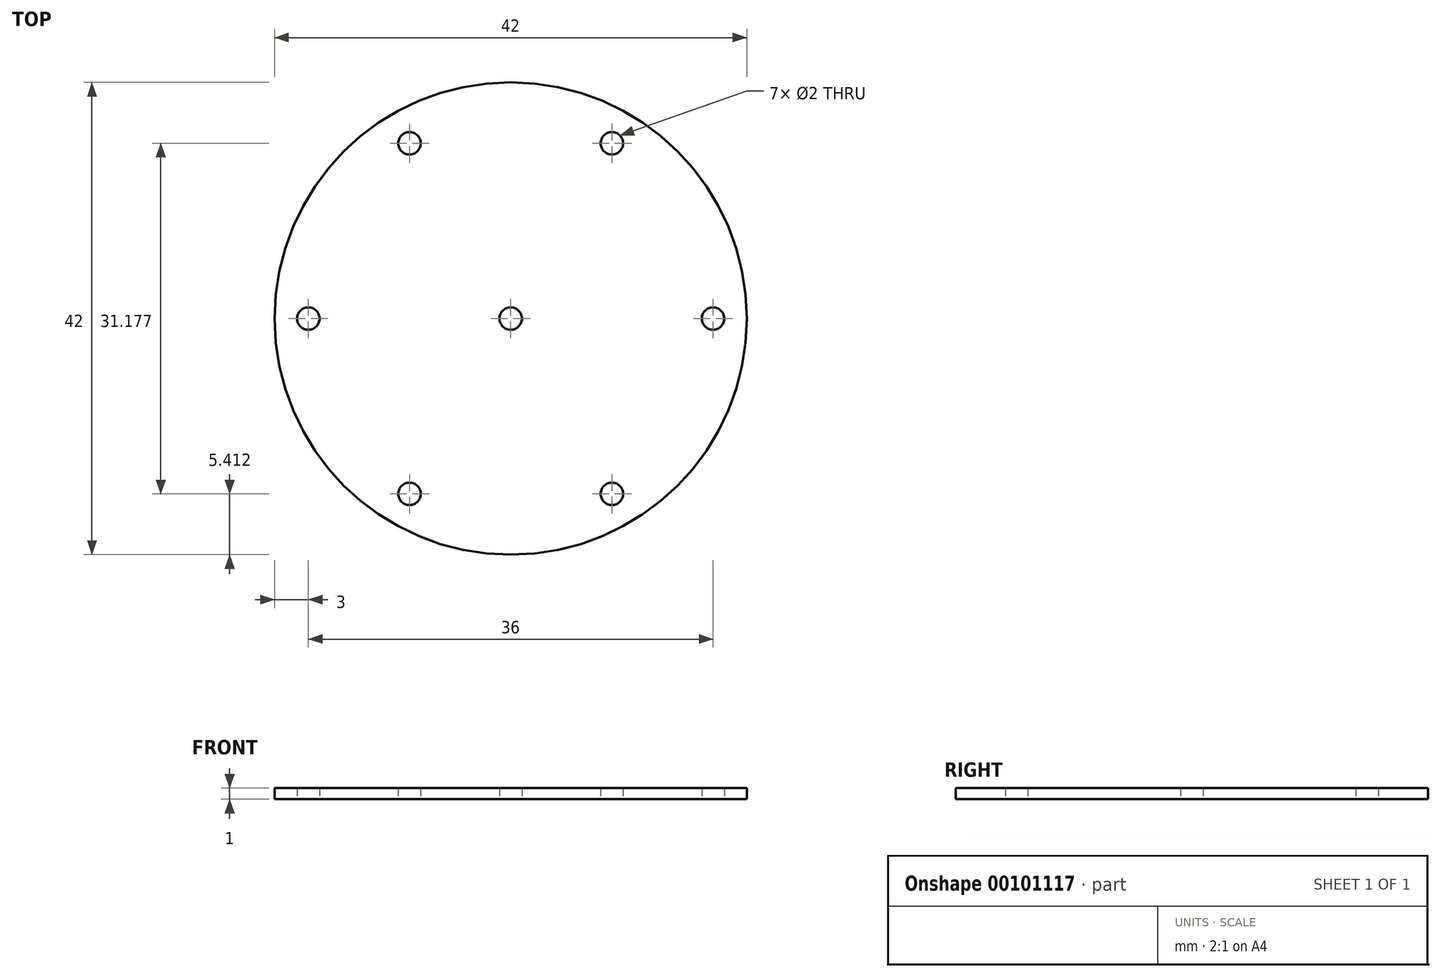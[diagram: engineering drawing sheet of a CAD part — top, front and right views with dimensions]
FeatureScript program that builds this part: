
annotation { "Feature Type Name" : "Feature", "Feature Type Description" : "" }
export const myFeature = defineFeature(function(context is Context, id is Id, definition is map)
    precondition{}
    {
        {
            var Q0;
            Q0=qCreatedBy(makeId("Top.planeOp"),FACE);
            var sketch = newSketch(context, id + "F0", { "sketchPlane" : qUnion([Q0])});
            skCircle(sketch, "E0", {"center": v(0, 0) * mm, "radius": 21 * mm});
            skPoint(sketch, "E1", {"position": v(-18, 0) * mm});
            skPoint(sketch, "E2.1.0", {"position": v(-9, -15.59) * mm});
            skPoint(sketch, "E2.2.0", {"position": v(9, -15.59) * mm});
            skPoint(sketch, "E2.3.0", {"position": v(18, 0) * mm});
            skPoint(sketch, "E2.4.0", {"position": v(9, 15.59) * mm});
            skPoint(sketch, "E2.5.0", {"position": v(-9, 15.59) * mm});
            skSolve(sketch);
        }
        {
            var Q0;
            Q0=makeQuery(id+"F0.imprint","IMPRINT",FACE,{"disambiguationData":[TD([[makeQuery(id+"F0.imprint","IMPRINT",EDGE,{"derivedFrom":sQuery(id+"F0.wireOp",EDGE,"E0")}),1.0]])]});
            var Q1;
            {var subQ0=sQuery(id+"F0.wireOp",EDGE,"3bcc4da2-44fa-43c9-b4fa-2db78715bdb7");Q1=makeQuery(id+"F0.imprint","IMPRINT",FACE,{"disambiguationData":[TD([[makeQuery(id+"F0.imprint","IMPRINT",EDGE,{"derivedFrom":subQ0}),1.0]])]});}
            var Q2;
            {var subQ0=sQuery(id+"F0.wireOp",EDGE,"ddd3eef2-9e28-40f6-aaa8-a0d2f989048d");Q2=makeQuery(id+"F0.imprint","IMPRINT",FACE,{"disambiguationData":[TD([[makeQuery(id+"F0.imprint","IMPRINT",EDGE,{"derivedFrom":subQ0}),-1.0]])]});}
            var Q3;
            Q3=makeQuery(id+"F0.imprint","IMPRINT",FACE,{"disambiguationData":[TD([[makeQuery(id+"F0.imprint","IMPRINT",EDGE,{"derivedFrom":sQuery(id+"F0.wireOp",EDGE,"UoSo9vnu-HFId-69mQ-OT0g-zSg1OUFx8jNl")}),1.0]])]});
            var Q4;
            Q4=makeQuery(id+"F0.imprint","IMPRINT",FACE,{"disambiguationData":[TD([[makeQuery(id+"F0.imprint","IMPRINT",EDGE,{"derivedFrom":sQuery(id+"F0.wireOp",EDGE,"0PuS1Hix-Aw6P-TIuu-lL9w-gV71d6cxZzEH")}),1.0]])]});
            extrude(context, id + "F1", {"entities" : qUnion([Q0, Q1, Q2, Q3, Q4]), "depth" : 1 * mm});
        }
        {
            var Q0;
            Q0=sQuery(id+"F0.wireOp",VERTEX,"E1");
            var Q1;
            Q1=sQuery(id+"F0.wireOp",VERTEX,"E2.3.0");
            var Q2;
            Q2=sQuery(id+"F0.wireOp",VERTEX,"E0.center");
            var Q3;
            Q3=sQuery(id+"F0.wireOp",VERTEX,"E2.1.0");
            var Q4;
            Q4=sQuery(id+"F0.wireOp",VERTEX,"E2.2.0");
            var Q5;
            Q5=sQuery(id+"F0.wireOp",VERTEX,"E2.4.0");
            var Q6;
            Q6=sQuery(id+"F0.wireOp",VERTEX,"E2.5.0");
            var Q7;
            Q7=makeQuery(id+"F1.opExtrude","SWEPT_BODY",BODY,{"disambiguationData":[OSD([sQuery(id+"F0.wireOp",EDGE,"d6273009-78ba-4e5d-af79-cc423ed6a4f3"),sQuery(id+"F0.wireOp",EDGE,"3bcc4da2-44fa-43c9-b4fa-2db78715bdb7"),sQuery(id+"F0.wireOp",EDGE,"ddd3eef2-9e28-40f6-aaa8-a0d2f989048d"),sQuery(id+"F0.wireOp",EDGE,"E0")])]});
            hole(context, id + "F2", {"style" : HoleStyle.SIMPLE, "endStyle" : HoleEndStyle.THROUGH, "oppositeDirection" : true, "holeDiameter" : 2 * mm, "locations" : qUnion([Q0, Q1, Q2, Q3, Q4, Q5, Q6]), "scope" : qUnion([Q7]), "isTappedThrough" : true});
        }
    });
